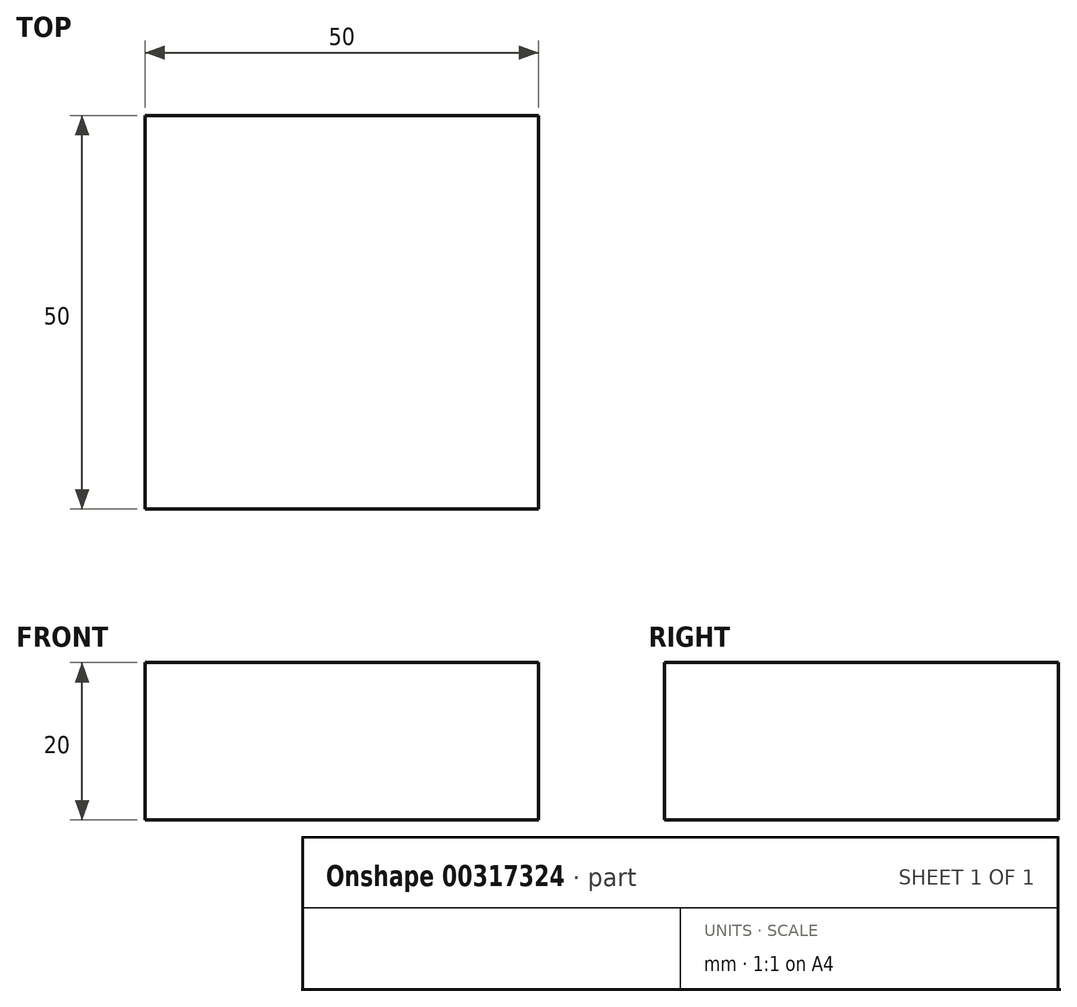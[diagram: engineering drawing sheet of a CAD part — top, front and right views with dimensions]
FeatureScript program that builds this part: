
annotation { "Feature Type Name" : "Feature", "Feature Type Description" : "" }
export const myFeature = defineFeature(function(context is Context, id is Id, definition is map)
    precondition{}
    {
        {
            var Q0;
            Q0=qCreatedBy(makeId("Right.planeOp"),FACE);
            var sketch = newSketch(context, id + "F0", { "sketchPlane" : qUnion([Q0])});
            skLineSegment(sketch, "E0.bottom", {"start": v(25, 10) * mm, "end": v(-25, 10) * mm});
            skLineSegment(sketch, "E0.top", {"start": v(25, -10) * mm, "end": v(-25, -10) * mm});
            skLineSegment(sketch, "E0.left", {"start": v(25, 10) * mm, "end": v(25, -10) * mm});
            skLineSegment(sketch, "E0.right", {"start": v(-25, 10) * mm, "end": v(-25, -10) * mm});
            skPoint(sketch, "E0.middle", {"position": v(0, 0) * mm});
            skSolve(sketch);
        }
        {
            var Q0;
            Q0=makeQuery(id+"F0.imprint","IMPRINT",FACE,{"disambiguationData":[TD([[makeQuery(id+"F0.imprint","IMPRINT",EDGE,{"derivedFrom":sQuery(id+"F0.wireOp",EDGE,"E0.bottom")}),1.0]])]});
            extrude(context, id + "F1", {"entities" : qUnion([Q0]), "depth" : 50 * mm});
        }
    });
